# Revit family: agtatec_Record_SldngDrset_D-STA_WallBased
name_source: partatom
category: Doors
revit_build: Autodesk Revit Architecture 2015 (Build: 20140606_1530(x64)
units: mm (PartAtom-declared; Revit-internal decimal feet)

## types (12) — shared parameters
AccessoryOptions = Contact manufacturer
AcousticRating = None
AlternativeDoorsetGlazing = Part of glazing spec
AntiFingerTrapRequirement = Yes
Assembly Code = B2030110
BIMObjectName = agtatec_Record_SlidingDoorset_D-STA_WallBased
CenterOfDoor = 1300.00 mm
ClearHeightOfPassage = 2187.00 mm
ClearanceZones = No
Colour = Customer specific
Configuration = 1 or 2
Construction Type = Automatic Sliding Door
Description = Automatic Sliding Door
DoorIncluded = Yes
DoorOpening = 0.00 mm
DoorSeal = yes
DoorsetFasteners = Screws
DoorsetOperation = Automatic
DriveUnit = agtatec_Record_Sliding Door, Sheet Metal (Painted Steel)
DriveUnitCenterDistance = 1365.00 mm
DriveUnitExtraWidthLeft = 0.00 mm
DriveUnitExtraWidthRight = 0.00 mm
DurationUnit = year
ElectronicLock = Yes
ExtraLeft = 0.00 mm
ExtraRight = 0.00 mm
ExtraWidthLeft = 0.00 mm
ExtraWidthRight = 0.00 mm
Finish = Powder coated, Anodized, customer specific
FireExit = No
FireRating = None
FloorGuide = agtatec_Record_Sliding Door, Stainless Steel
FrameMaterial = Aluminium
FrameProfile = Aluminium
FrameSeal = Yes
GlassLayers = 2
GlassThickness1 = 6 mm (default)
GlassThickness2 = 6 mm (default)
GlassType = Part of glazing spec
GlazingAreaFraction = Depends on size. Can be calculated
HandicapAccessible = Yes
HasDrive = Yes
IfcExportAs = IfcDoorStyle
IfcExportType = Door
InnerPanelWidth = 632.00 mm
IsExternal = Yes
LeafColourOptions = All RAL, customer specific
ManufacturerName = Record
ManufacturerURL = www.agta-record.com
Material = Aluminium
Model = record Standard Linear Slider
ModelReference = Depends on the configuration
MountingProfileLeft = No
MountingProfileRight = No
NBSDescription = Sliding Doorset
NBSReference = 25-50-20/175
Name = SldngDrset_D-STA_WallBased_Record
NominalLength = 0.00 mm
Offset = 0.00 mm
OffsetFromInteriorWallFace(OnlyApplicableForTypesWithTwoSidePanels) = 0.00 mm
OffsetFromWallSide = 0.00 mm
OffsetFromWallTop = 0.00 mm
OpeningAxis = 1300.00 mm
OpeningWidth = 1200.00 mm
OpeningWidthInWall = 1148.00 mm
PanelFill = agtatec_Record_Sliding Door, Laminated Safety Glass (Clear)
PanelFrames = agtatec_Record_Sliding Door, Aluminium
PanelHeight = 2200.00 mm
PassageMountingProfile(OnlyApplicableForTypesWithTwoSidePanels) = No
ProductInformation = www.agta-record.com
ReferenceStandard = EN16005, EN16361, DIN 18650, etc.
ReplacementCost = Depends on the configuration and door type
SecurityRating = None
SelfClosing = Yes
ServiceLifeDuration = 10-15 years
Shape = Rectangular
SidePanelMinimumStandard = 632.00 mm
SidePanelWidthLeft = 700.00 mm
SidePanelWidthRight = 700.00 mm
SmokeStop = No
SupportLength = 2600.00 mm
Thickness = 0.00 mm
ThresholdRequired = Yes
ThresholdStripping = No additional required, part of the doorset
URL = www.agta-record.com
Uniclass2 = Ss_25_30_20_77
Version = Version 1.0
WallMountingProfile = Yes
WarrantyDescription = Depends on country
WarrantyDurationLabour = Depends on country
WarrantyDurationParts = Depends on country
WarrantyDurationUnit = Depends on country
WarrantyGuarantorLabour = Local door manufacturer
WarrantyGuarantorParts = Local door manufacturer
Weight = Depends on configuration and size
WithDriveCladding = Yes
WithinStandardSizes = Yes
WithoutDriveCladding(OnlyApplicableForTypesWithoutSidePanels) = No
zero-valued in all types: Cost, ThermalTransmittance

## per-type parameters (varying)
| type | DriveUnitHeight | Height | LeftPanel | NominalHeight | NominalWidth | RightPanel | Rough Height | Rough Width | SideVoidLeft | SideVoidRight | TotalHeight | TotalWidth | Width | WithSidePanels |
| D-STA 150 mm drive unit height - side panel left | 150.00 mm | 2337.00 mm | Yes | 2337.00 mm | 1954.50 mm | No | 2343.00 mm | 1960.50 mm | 653.00 mm | 0.00 mm | 2337.00 mm | 1954.50 mm | 1954.50 mm | No |
| D-STA 150 mm drive unit height - side panel right | 150.00 mm | 2337.00 mm | No | 2337.00 mm | 1954.50 mm | Yes | 2343.00 mm | 1960.50 mm | 0.00 mm | 653.00 mm | 2337.00 mm | 1954.50 mm | 1954.50 mm | No |
| D-STA 150 mm drive unit height - with two side panels | 150.00 mm | 2337.00 mm | Yes | 2337.00 mm | 2600.00 mm | Yes | 2343.00 mm | 2606.00 mm | 653.00 mm | 653.00 mm | 2337.00 mm | 2600.00 mm | 2600.00 mm | Yes |
| D-STA 150 mm drive unit height - without side panels | 150.00 mm | 2337.00 mm | No | 2337.00 mm | 1309.00 mm | No | 2343.00 mm | 1315.00 mm | 0.00 mm | 0.00 mm | 2337.00 mm | 1309.00 mm | 1309.00 mm | No |
| D-STA 200 mm drive unit height - side panel left | 200.00 mm | 2387.00 mm | Yes | 2387.00 mm | 1954.50 mm | No | 2393.00 mm | 1960.50 mm | 653.00 mm | 0.00 mm | 2387.00 mm | 1954.50 mm | 1954.50 mm | No |
| D-STA 200 mm drive unit height - side panel right | 200.00 mm | 2387.00 mm | No | 2387.00 mm | 1954.50 mm | Yes | 2393.00 mm | 1960.50 mm | 0.00 mm | 653.00 mm | 2387.00 mm | 1954.50 mm | 1954.50 mm | No |
| D-STA 200 mm drive unit height - with two side panels | 200.00 mm | 2387.00 mm | Yes | 2387.00 mm | 2600.00 mm | Yes | 2393.00 mm | 2606.00 mm | 653.00 mm | 653.00 mm | 2387.00 mm | 2600.00 mm | 2600.00 mm | Yes |
| D-STA 200 mm drive unit height - without side panels | 200.00 mm | 2387.00 mm | No | 2387.00 mm | 1309.00 mm | No | 2393.00 mm | 1315.00 mm | 0.00 mm | 0.00 mm | 2387.00 mm | 1309.00 mm | 1309.00 mm | No |
| D-STA 108 mm drive unit height - side panel left | 108.00 mm | 2295.00 mm | Yes | 2295.00 mm | 1954.50 mm | No | 2301.00 mm | 1960.50 mm | 653.00 mm | 0.00 mm | 2295.00 mm | 1954.50 mm | 1954.50 mm | No |
| D-STA 108 mm drive unit height - side panel right | 108.00 mm | 2295.00 mm | No | 2295.00 mm | 1954.50 mm | Yes | 2301.00 mm | 1960.50 mm | 0.00 mm | 653.00 mm | 2295.00 mm | 1954.50 mm | 1954.50 mm | No |
| D-STA 108 mm drive unit height - with two side panels | 108.00 mm | 2295.00 mm | Yes | 2295.00 mm | 2600.00 mm | Yes | 2301.00 mm | 2606.00 mm | 653.00 mm | 653.00 mm | 2295.00 mm | 2600.00 mm | 2600.00 mm | Yes |
| D-STA 108 mm drive unit height - without side panels | 108.00 mm | 2295.00 mm | No | 2295.00 mm | 1309.00 mm | No | 2301.00 mm | 1315.00 mm | 0.00 mm | 0.00 mm | 2295.00 mm | 1309.00 mm | 1309.00 mm | No |

## geometry (parser evidence)
native form markers: Sweep x14
no freeform markers — native parametric forms only
